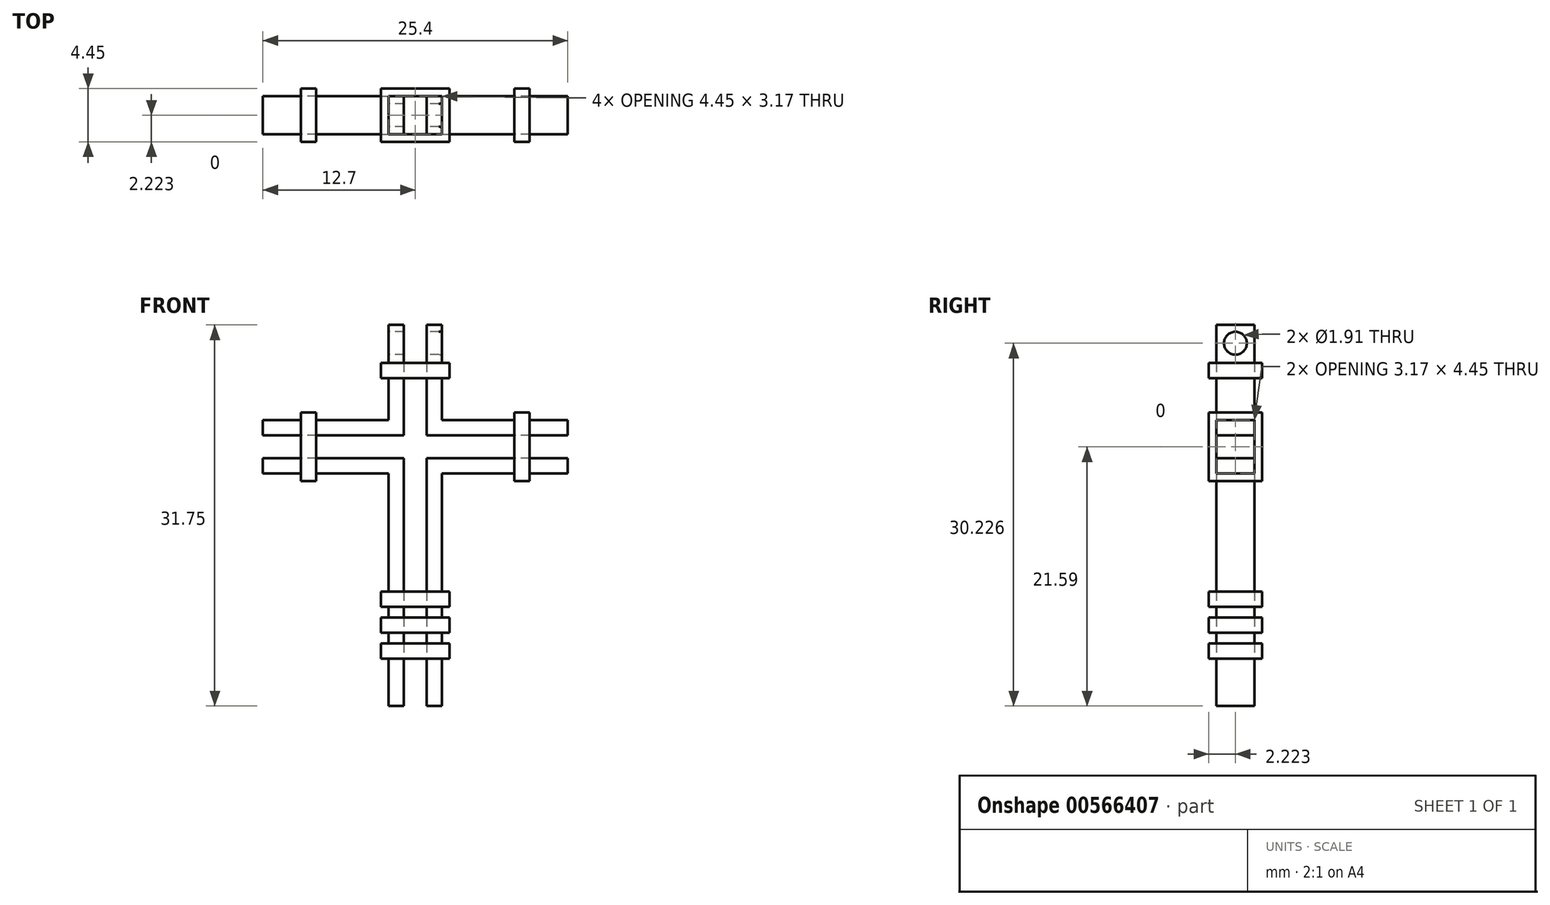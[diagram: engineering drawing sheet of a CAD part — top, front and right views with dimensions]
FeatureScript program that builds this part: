
annotation { "Feature Type Name" : "Feature", "Feature Type Description" : "" }
export const myFeature = defineFeature(function(context is Context, id is Id, definition is map)
    precondition{}
    {
        {
            var Q0;
            Q0=qCreatedBy(makeId("Front.planeOp"),FACE);
            var sketch = newSketch(context, id + "F0", { "sketchPlane" : qUnion([Q0])});
            skLineSegment(sketch, "E0.bottom", {"start": v(-2.22, 10.16) * mm, "end": v(2.22, 10.16) * mm});
            skLineSegment(sketch, "E0.top", {"start": v(-2.22, -21.59) * mm, "end": v(2.22, -21.59) * mm});
            skLineSegment(sketch, "E0.left", {"start": v(-2.22, 10.16) * mm, "end": v(-2.22, 2.22) * mm});
            skLineSegment(sketch, "E0.right", {"start": v(2.22, 10.16) * mm, "end": v(2.22, 2.22) * mm});
            skLineSegment(sketch, "E1.bottom", {"start": v(-12.7, 2.22) * mm, "end": v(-2.22, 2.22) * mm});
            skLineSegment(sketch, "E1.top", {"start": v(-12.7, -2.22) * mm, "end": v(-2.22, -2.22) * mm});
            skLineSegment(sketch, "E1.left", {"start": v(-12.7, 2.22) * mm, "end": v(-12.7, -2.22) * mm});
            skLineSegment(sketch, "E1.right", {"start": v(12.7, 2.22) * mm, "end": v(12.7, -2.22) * mm});
            skLineSegment(sketch, "E2.trimOffspring", {"start": v(2.22, 2.22) * mm, "end": v(12.7, 2.22) * mm});
            skLineSegment(sketch, "E3.trimOffspring", {"start": v(2.22, -2.22) * mm, "end": v(2.22, -21.59) * mm});
            skLineSegment(sketch, "E4.trimOffspring", {"start": v(2.22, -2.22) * mm, "end": v(12.7, -2.22) * mm});
            skLineSegment(sketch, "E5.trimOffspring", {"start": v(-2.22, -2.22) * mm, "end": v(-2.22, -21.59) * mm});
            skSolve(sketch);
        }
        {
            var Q0;
            Q0=makeQuery(id+"F0.imprint","IMPRINT",FACE,{"disambiguationData":[TD([[makeQuery(id+"F0.imprint","IMPRINT",EDGE,{"derivedFrom":sQuery(id+"F0.wireOp",EDGE,"E0.bottom")}),-1.0]])]});
            extrude(context, id + "F1", {"entities" : qUnion([Q0]), "depth" : 3.17 * mm, "offsetDistance" : 25.4 * mm});
        }
        {
            var Q0;
            Q0=qCreatedBy(makeId("Front.planeOp"),FACE);
            var sketch = newSketch(context, id + "F2", { "sketchPlane" : qUnion([Q0])});
            skLineSegment(sketch, "E6.bottom", {"start": v(0.95, -22.86) * mm, "end": v(-0.95, -22.86) * mm});
            skLineSegment(sketch, "E6.top", {"start": v(0.95, 22.86) * mm, "end": v(-0.95, 22.86) * mm});
            skLineSegment(sketch, "E6.left", {"start": v(0.95, -22.86) * mm, "end": v(0.95, -0.95) * mm});
            skLineSegment(sketch, "E6.right", {"start": v(-0.95, -22.86) * mm, "end": v(-0.95, -0.95) * mm});
            skPoint(sketch, "E6.middle", {"position": v(0, 0) * mm});
            skLineSegment(sketch, "E7.bottom", {"start": v(15.88, -0.95) * mm, "end": v(0.95, -0.95) * mm});
            skLineSegment(sketch, "E7.top", {"start": v(15.88, 0.95) * mm, "end": v(0.95, 0.95) * mm});
            skLineSegment(sketch, "E7.left", {"start": v(15.88, -0.95) * mm, "end": v(15.88, 0.95) * mm});
            skLineSegment(sketch, "E7.right", {"start": v(-15.88, -0.95) * mm, "end": v(-15.88, 0.95) * mm});
            skLineSegment(sketch, "E8.trimOffspring", {"start": v(0.95, 0.95) * mm, "end": v(0.95, 22.86) * mm});
            skLineSegment(sketch, "E9.trimOffspring", {"start": v(-0.95, 0.95) * mm, "end": v(-15.88, 0.95) * mm});
            skLineSegment(sketch, "E10.trimOffspring", {"start": v(-0.95, 0.95) * mm, "end": v(-0.95, 22.86) * mm});
            skLineSegment(sketch, "E11.trimOffspring", {"start": v(-0.95, -0.95) * mm, "end": v(-15.88, -0.95) * mm});
            skSolve(sketch);
        }
        {
            var Q0;
            Q0=makeQuery(id+"F2.imprint","IMPRINT",FACE,{"disambiguationData":[TD([[makeQuery(id+"F2.imprint","IMPRINT",EDGE,{"derivedFrom":sQuery(id+"F2.wireOp",EDGE,"E6.bottom")}),-1.0]])]});
            extrude(context, id + "F3", {"entities" : qUnion([Q0]), "operationType" : NewBodyOperationType.REMOVE, "endBound" : BoundingType.THROUGH_ALL, "depth" : 25.4 * mm, "offsetDistance" : 25.4 * mm});
        }
        {
            var Q0;
            Q0=qCreatedBy(makeId("Front.planeOp"),FACE);
            cPlane(context, id + "F4", {"entities" : qUnion([Q0]), "cplaneType" : CPlaneType.OFFSET, "offset" : 0.64 * mm, "oppositeDirection" : true, "width" : 152.4 * mm, "height" : 152.4 * mm});
        }
        {
            var Q0;
            Q0=qCreatedBy(id+"F4.planeOp",FACE);
            var sketch = newSketch(context, id + "F5", { "sketchPlane" : qUnion([Q0])});
            skLineSegment(sketch, "E12.bottom", {"start": v(-8.26, 2.86) * mm, "end": v(-9.52, 2.86) * mm});
            skLineSegment(sketch, "E12.top", {"start": v(-8.26, -2.86) * mm, "end": v(-9.52, -2.86) * mm});
            skLineSegment(sketch, "E12.left", {"start": v(-8.26, 2.86) * mm, "end": v(-8.26, -2.86) * mm});
            skLineSegment(sketch, "E12.right", {"start": v(-9.52, 2.86) * mm, "end": v(-9.52, -2.86) * mm});
            skPoint(sketch, "E12.middle", {"position": v(-8.9, 0) * mm});
            skLineSegment(sketch, "E13.MirrorCS", {"start": v(8.26, 2.86) * mm, "end": v(8.26, -2.86) * mm});
            skLineSegment(sketch, "E14.MirrorCS", {"start": v(8.26, 2.86) * mm, "end": v(9.52, 2.86) * mm});
            skLineSegment(sketch, "E15.MirrorCS", {"start": v(9.52, 2.86) * mm, "end": v(9.52, -2.86) * mm});
            skLineSegment(sketch, "E16.MirrorCS", {"start": v(8.26, -2.86) * mm, "end": v(9.52, -2.86) * mm});
            skLineSegment(sketch, "E17.bottom", {"start": v(2.86, 5.72) * mm, "end": v(-2.86, 5.72) * mm});
            skLineSegment(sketch, "E17.top", {"start": v(2.86, 6.99) * mm, "end": v(-2.86, 6.99) * mm});
            skLineSegment(sketch, "E17.left", {"start": v(2.86, 5.72) * mm, "end": v(2.86, 6.99) * mm});
            skLineSegment(sketch, "E17.right", {"start": v(-2.86, 5.72) * mm, "end": v(-2.86, 6.99) * mm});
            skPoint(sketch, "E17.middle", {"position": v(0, 6.35) * mm});
            skLineSegment(sketch, "E18.bottom", {"start": v(2.86, -12.07) * mm, "end": v(-2.86, -12.07) * mm});
            skLineSegment(sketch, "E18.top", {"start": v(2.86, -13.34) * mm, "end": v(-2.86, -13.34) * mm});
            skLineSegment(sketch, "E18.left", {"start": v(2.86, -12.07) * mm, "end": v(2.86, -13.34) * mm});
            skLineSegment(sketch, "E18.right", {"start": v(-2.86, -12.07) * mm, "end": v(-2.86, -13.34) * mm});
            skPoint(sketch, "E18.middle", {"position": v(0, -12.7) * mm});
            skLineSegment(sketch, "E19.bottom", {"start": v(2.86, -15.5) * mm, "end": v(-2.86, -15.5) * mm});
            skLineSegment(sketch, "E19.top", {"start": v(2.86, -14.22) * mm, "end": v(-2.86, -14.22) * mm});
            skLineSegment(sketch, "E19.left", {"start": v(2.86, -15.5) * mm, "end": v(2.86, -14.22) * mm});
            skLineSegment(sketch, "E19.right", {"start": v(-2.86, -15.5) * mm, "end": v(-2.86, -14.22) * mm});
            skPoint(sketch, "E19.middle", {"position": v(0, -14.86) * mm});
            skLineSegment(sketch, "E20.bottom", {"start": v(2.86, -17.65) * mm, "end": v(-2.86, -17.65) * mm});
            skLineSegment(sketch, "E20.top", {"start": v(2.86, -16.38) * mm, "end": v(-2.86, -16.38) * mm});
            skLineSegment(sketch, "E20.left", {"start": v(2.86, -17.65) * mm, "end": v(2.86, -16.38) * mm});
            skLineSegment(sketch, "E20.right", {"start": v(-2.86, -17.65) * mm, "end": v(-2.86, -16.38) * mm});
            skPoint(sketch, "E20.middle", {"position": v(0, -17.02) * mm});
            skSolve(sketch);
        }
        {
            var Q0;
            Q0 = qSketchRegion(id + "F5", true);
            extrude(context, id + "F6", {"entities" : qUnion([Q0]), "operationType" : NewBodyOperationType.ADD, "depth" : 4.44 * mm, "offsetDistance" : 25.4 * mm});
        }
        {
            var Q0;
            Q0=qCreatedBy(makeId("Top.planeOp"),FACE);
            var sketch = newSketch(context, id + "F7", { "sketchPlane" : qUnion([Q0])});
            skLineSegment(sketch, "E21.bottom", {"start": v(-0.95, -3.18) * mm, "end": v(0.95, -3.18) * mm});
            skLineSegment(sketch, "E21.top", {"start": v(-0.95, 0) * mm, "end": v(0.95, 0) * mm});
            skLineSegment(sketch, "E21.left", {"start": v(-0.95, -3.18) * mm, "end": v(-0.95, 0) * mm});
            skLineSegment(sketch, "E21.right", {"start": v(0.95, -3.18) * mm, "end": v(0.95, 0) * mm});
            skSolve(sketch);
        }
        {
            var Q0;
            Q0 = qSketchRegion(id + "F7", true);
            extrude(context, id + "F8", {"entities" : qUnion([Q0]), "operationType" : NewBodyOperationType.REMOVE, "endBound" : BoundingType.SYMMETRIC, "depth" : 50.8 * mm, "offsetDistance" : 25.4 * mm});
        }
        {
            var Q0;
            Q0=qCreatedBy(makeId("Right.planeOp"),FACE);
            var sketch = newSketch(context, id + "F9", { "sketchPlane" : qUnion([Q0])});
            skLineSegment(sketch, "E22.bottom", {"start": v(-3.18, -0.95) * mm, "end": v(0, -0.95) * mm});
            skLineSegment(sketch, "E22.top", {"start": v(-3.18, 0.95) * mm, "end": v(0, 0.95) * mm});
            skLineSegment(sketch, "E22.left", {"start": v(-3.18, -0.95) * mm, "end": v(-3.18, 0.95) * mm});
            skLineSegment(sketch, "E22.right", {"start": v(0, -0.95) * mm, "end": v(0, 0.95) * mm});
            skSolve(sketch);
        }
        {
            var Q0;
            Q0 = qSketchRegion(id + "F9", true);
            extrude(context, id + "F10", {"entities" : qUnion([Q0]), "operationType" : NewBodyOperationType.REMOVE, "endBound" : BoundingType.SYMMETRIC, "depth" : 38.1 * mm, "offsetDistance" : 25.4 * mm});
        }
        {
            var Q0;
            {var subQ0=sQuery(id+"F0.wireOp",EDGE,"E0.bottom");var subQ10=sQuery(id+"F0.wireOp",EDGE,"E0.left");Q0=makeQuery(id+"F6.boolean.opBoolean","SPLIT",FACE,{"disambiguationData":[TD([makeQuery(id+"F1.opExtrude","SWEPT_FACE",FACE,{"disambiguationData":[OSD([subQ0])]})])],"derivedFrom":makeQuery(id+"F1.opExtrude","SWEPT_FACE",FACE,{"disambiguationData":[OSD([subQ10])]})});}
            var sketch = newSketch(context, id + "F11", { "sketchPlane" : qUnion([Q0])});
            skCircle(sketch, "E23", {"center": v(1.59, 8.64) * mm, "radius": 0.95 * mm});
            skSolve(sketch);
        }
        {
            var Q0;
            Q0 = qSketchRegion(id + "F11", true);
            extrude(context, id + "F12", {"entities" : qUnion([Q0]), "operationType" : NewBodyOperationType.REMOVE, "endBound" : BoundingType.THROUGH_ALL, "oppositeDirection" : true, "depth" : 25.4 * mm, "offsetDistance" : 25.4 * mm});
        }
        {
            var Q0;
            Q0=makeQuery(id+"F12.boolean.opBoolean","COPY",EDGE,{"derivedFrom":makeQuery(id+"F12.opExtrude","CAP_EDGE",EDGE,{"disambiguationData":[OSD([sQuery(id+"F11.wireOp",EDGE,"E23")])],"isStart":true})});
            var Q1;
            {var subQ0=sQuery(id+"F0.wireOp",EDGE,"E0.bottom");var subQ9=sQuery(id+"F0.wireOp",EDGE,"E0.right");Q1=makeQuery(id+"F12.boolean.opBoolean","INTERSECT",EDGE,{"derivedFrom":[makeQuery(id+"F6.boolean.opBoolean","SPLIT",FACE,{"disambiguationData":[TD([makeQuery(id+"F1.opExtrude","SWEPT_FACE",FACE,{"disambiguationData":[OSD([subQ0])]})])],"derivedFrom":makeQuery(id+"F1.opExtrude","SWEPT_FACE",FACE,{"disambiguationData":[OSD([subQ9])]})}),makeQuery(id+"F12.opExtrude","SWEPT_FACE",FACE,{"disambiguationData":[OSD([sQuery(id+"F11.wireOp",EDGE,"E23")])]})]});}
            fillet(context, id + "F13", {"entities" : qUnion([Q0, Q1]), "radius" : 0.25 * mm, "tangentPropagation" : true, "allowEdgeOverflow" : false});
        }
    });
